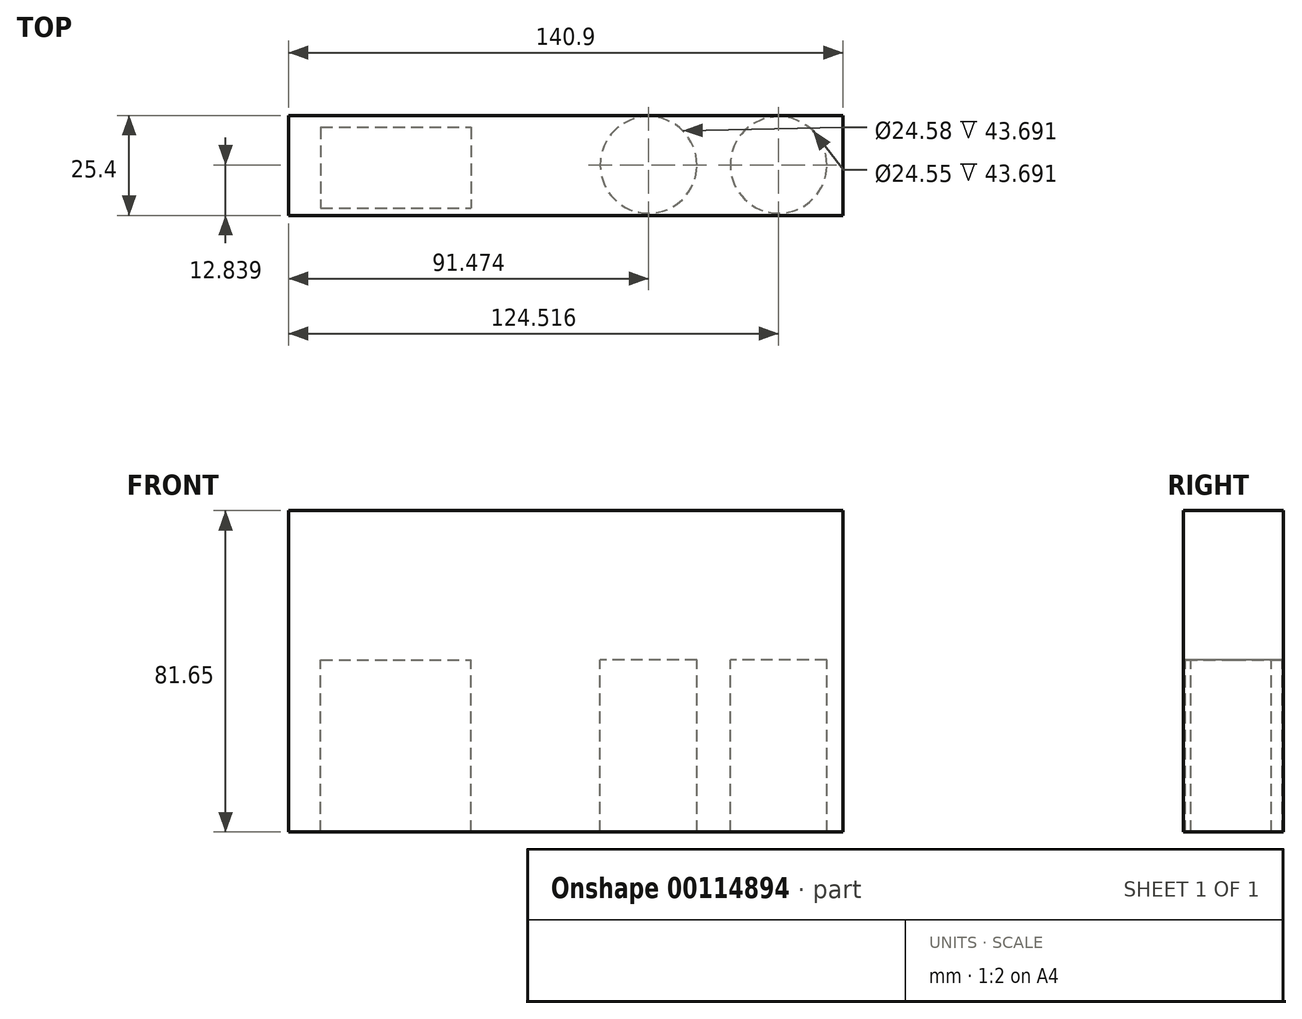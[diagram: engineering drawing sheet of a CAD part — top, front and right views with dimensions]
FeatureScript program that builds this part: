
annotation { "Feature Type Name" : "Feature", "Feature Type Description" : "" }
export const myFeature = defineFeature(function(context is Context, id is Id, definition is map)
    precondition{}
    {
        {
            var Q0;
            Q0=qCreatedBy(makeId("Front.planeOp"),FACE);
            var sketch = newSketch(context, id + "F0", { "sketchPlane" : qUnion([Q0])});
            skLineSegment(sketch, "E0.bottom", {"start": v(-68, 37.96) * mm, "end": v(72.91, 37.96) * mm});
            skLineSegment(sketch, "E0.top", {"start": v(-68, -43.7) * mm, "end": v(72.91, -43.7) * mm});
            skLineSegment(sketch, "E0.left", {"start": v(-68, 37.96) * mm, "end": v(-68, -43.7) * mm});
            skLineSegment(sketch, "E0.right", {"start": v(72.91, 37.96) * mm, "end": v(72.91, -43.7) * mm});
            skSolve(sketch);
        }
        {
            var Q0;
            Q0=makeQuery(id+"F0.imprint","IMPRINT",FACE,{"disambiguationData":[TD([[makeQuery(id+"F0.imprint","IMPRINT",EDGE,{"derivedFrom":sQuery(id+"F0.wireOp",EDGE,"E0.bottom")}),-1.0]])]});
            extrude(context, id + "F1", {"entities" : qUnion([Q0]), "depth" : 25.4 * mm});
        }
        {
            var Q0;
            Q0=qCreatedBy(makeId("Top.planeOp"),FACE);
            var sketch = newSketch(context, id + "F2", { "sketchPlane" : qUnion([Q0])});
            skCircle(sketch, "E1", {"center": v(56.53, -12.56) * mm, "radius": 12.27 * mm});
            skCircle(sketch, "E2", {"center": v(23.48, -12.56) * mm, "radius": 12.29 * mm});
            skLineSegment(sketch, "E3.bottom", {"start": v(-59.8, -3) * mm, "end": v(-21.57, -3) * mm});
            skLineSegment(sketch, "E3.top", {"start": v(-59.8, -23.48) * mm, "end": v(-21.57, -23.48) * mm});
            skLineSegment(sketch, "E3.left", {"start": v(-59.8, -3) * mm, "end": v(-59.8, -23.48) * mm});
            skLineSegment(sketch, "E3.right", {"start": v(-21.57, -3) * mm, "end": v(-21.57, -23.48) * mm});
            skSolve(sketch);
        }
        {
            var Q0;
            Q0 = qSketchRegion(id + "F2", true);
            extrude(context, id + "F3", {"entities" : qUnion([Q0]), "operationType" : NewBodyOperationType.REMOVE, "endBound" : BoundingType.THROUGH_ALL, "oppositeDirection" : true, "depth" : 25.4 * mm});
        }
    });
